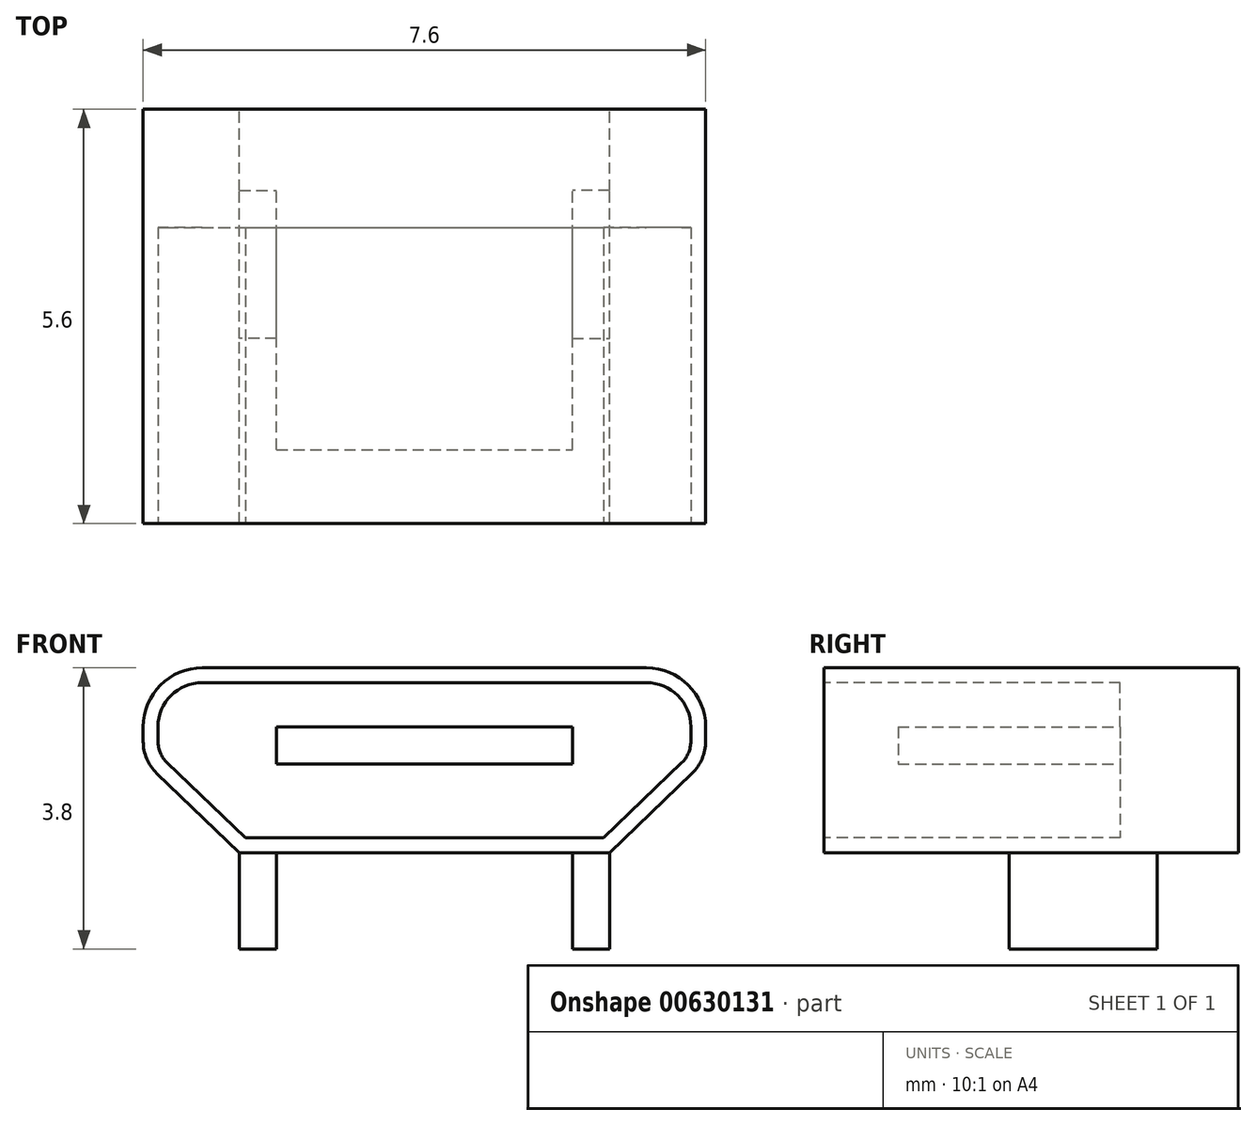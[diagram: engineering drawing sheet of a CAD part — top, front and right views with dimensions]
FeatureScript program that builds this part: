
annotation { "Feature Type Name" : "Feature", "Feature Type Description" : "" }
export const myFeature = defineFeature(function(context is Context, id is Id, definition is map)
    precondition{}
    {
        {
            var Q0;
            Q0=qCreatedBy(makeId("Front.planeOp"),FACE);
            var sketch = newSketch(context, id + "F0", { "sketchPlane" : qUnion([Q0])});
            skLineSegment(sketch, "E0.bottom", {"start": v(0, 0) * mm, "end": v(7.6, 0) * mm, "construction": true});
            skLineSegment(sketch, "E0.top", {"start": v(0, 2.5) * mm, "end": v(7.6, 2.5) * mm, "construction": true});
            skLineSegment(sketch, "E0.left", {"start": v(0, 0) * mm, "end": v(0, 2.5) * mm, "construction": true});
            skLineSegment(sketch, "E0.right", {"start": v(7.6, 0) * mm, "end": v(7.6, 2.5) * mm, "construction": true});
            skLineSegment(sketch, "E1", {"start": v(0, 1.25) * mm, "end": v(1.3, 0) * mm});
            skLineSegment(sketch, "E2", {"start": v(7.6, 1.25) * mm, "end": v(6.3, 0) * mm});
            skLineSegment(sketch, "E3", {"start": v(0, 1.25) * mm, "end": v(0, 2.5) * mm});
            skLineSegment(sketch, "E4", {"start": v(0, 2.5) * mm, "end": v(7.6, 2.5) * mm});
            skLineSegment(sketch, "E5", {"start": v(7.6, 2.5) * mm, "end": v(7.6, 1.25) * mm});
            skLineSegment(sketch, "E6", {"start": v(1.3, 0) * mm, "end": v(6.3, 0) * mm});
            skSolve(sketch);
        }
        {
            var Q0;
            Q0=qSketchRegion(id+"F0",true);
            extrude(context, id + "F1", {"entities" : qUnion([Q0]), "depth" : 5.6 * mm});
        }
        {
            var Q0;
            Q0=makeQuery(id+"F1.opExtrude","SWEPT_EDGE",EDGE,{"disambiguationData":[OSD([sQuery(id+"F0.wireOp",EDGE,"E3"),sQuery(id+"F0.wireOp",EDGE,"E4")])]});
            var Q1;
            Q1=makeQuery(id+"F1.opExtrude","SWEPT_EDGE",EDGE,{"disambiguationData":[OSD([sQuery(id+"F0.wireOp",EDGE,"E4"),sQuery(id+"F0.wireOp",EDGE,"E5")])]});
            fillet(context, id + "F2", {"entities" : qUnion([Q0, Q1]), "radius" : 0.8 * mm, "tangentPropagation" : true, "allowEdgeOverflow" : false});
        }
        {
            var Q0;
            Q0=makeQuery(id+"F1.opExtrude","SWEPT_EDGE",EDGE,{"disambiguationData":[OSD([sQuery(id+"F0.wireOp",EDGE,"E1"),sQuery(id+"F0.wireOp",EDGE,"E3")])]});
            var Q1;
            Q1=makeQuery(id+"F1.opExtrude","SWEPT_EDGE",EDGE,{"disambiguationData":[OSD([sQuery(id+"F0.wireOp",EDGE,"E2"),sQuery(id+"F0.wireOp",EDGE,"E5")])]});
            fillet(context, id + "F3", {"entities" : qUnion([Q0, Q1]), "radius" : 0.6 * mm, "tangentPropagation" : true, "allowEdgeOverflow" : false});
        }
        {
            var Q0;
            Q0=makeQuery(id+"F1.opExtrude","SWEPT_FACE",FACE,{"disambiguationData":[OSD([sQuery(id+"F0.wireOp",EDGE,"E6")])]});
            var sketch = newSketch(context, id + "F4", { "sketchPlane" : qUnion([Q0])});
            skLineSegment(sketch, "E7.right", {"start": v(1.8, 3.1) * mm, "end": v(1.8, 1.1) * mm});
            skLineSegment(sketch, "E8.top", {"start": v(6.3, 1.1) * mm, "end": v(5.8, 1.1) * mm});
            skLineSegment(sketch, "E8.right", {"start": v(5.8, 3.1) * mm, "end": v(5.8, 1.1) * mm});
            skLineSegment(sketch, "E9", {"start": v(1.8, 3.1) * mm, "end": v(1.3, 3.1) * mm});
            skLineSegment(sketch, "E10", {"start": v(5.8, 3.1) * mm, "end": v(6.3, 3.1) * mm});
            skLineSegment(sketch, "E11", {"start": v(6.3, 3.1) * mm, "end": v(6.3, 1.1) * mm});
            skLineSegment(sketch, "E12", {"start": v(1.3, 3.1) * mm, "end": v(1.3, 1.1) * mm});
            skLineSegment(sketch, "E13", {"start": v(1.3, 1.1) * mm, "end": v(1.8, 1.1) * mm});
            skSolve(sketch);
        }
        {
            var Q0;
            Q0=qSketchRegion(id+"F4",true);
            extrude(context, id + "F5", {"entities" : qUnion([Q0]), "operationType" : NewBodyOperationType.ADD, "depth" : 1.3 * mm});
        }
        {
            var Q0;
            Q0=makeQuery(id+"F5.boolean.opBoolean","MERGE",FACE,{"derivedFrom":[makeQuery(id+"F1.opExtrude","CAP_FACE",FACE,{"disambiguationData":[OSD([sQuery(id+"F0.wireOp",EDGE,"E1"),sQuery(id+"F0.wireOp",EDGE,"E2"),sQuery(id+"F0.wireOp",EDGE,"E3"),sQuery(id+"F0.wireOp",EDGE,"E4"),sQuery(id+"F0.wireOp",EDGE,"E5"),sQuery(id+"F0.wireOp",EDGE,"E6")])],"isStart":false}),makeQuery(id+"F5.opExtrude","SWEPT_FACE",FACE,{"disambiguationData":[OSD([sQuery(id+"F4.wireOp",EDGE,"E7.bottom")])]}),makeQuery(id+"F5.opExtrude","SWEPT_FACE",FACE,{"disambiguationData":[OSD([sQuery(id+"F4.wireOp",EDGE,"E8.bottom")])]})]});
            var sketch = newSketch(context, id + "F6", { "sketchPlane" : qUnion([Q0])});
            skLineSegment(sketch, "E14", {"start": v(0.8, 2.3) * mm, "end": v(6.8, 2.3) * mm});
            skLineSegment(sketch, "E15", {"start": v(1.38, 0.2) * mm, "end": v(6.22, 0.2) * mm});
            skArc(sketch, "E16", {"start": v(0.8, 2.3) * mm, "mid": v(0.38, 2.12) * mm, "end": v(0.2, 1.7) * mm});
            skArc(sketch, "E17", {"start": v(7.4, 1.7) * mm, "mid": v(7.22, 2.12) * mm, "end": v(6.8, 2.3) * mm});
            skLineSegment(sketch, "E18", {"start": v(0.32, 1.22) * mm, "end": v(1.38, 0.2) * mm});
            skArc(sketch, "E19", {"start": v(0.2, 1.5) * mm, "mid": v(0.23, 1.35) * mm, "end": v(0.32, 1.22) * mm});
            skArc(sketch, "E20", {"start": v(7.28, 1.22) * mm, "mid": v(7.37, 1.35) * mm, "end": v(7.4, 1.5) * mm});
            skLineSegment(sketch, "E21", {"start": v(7.4, 1.7) * mm, "end": v(7.4, 1.5) * mm});
            skLineSegment(sketch, "E22", {"start": v(7.28, 1.22) * mm, "end": v(6.22, 0.2) * mm});
            skLineSegment(sketch, "E23", {"start": v(0.2, 1.7) * mm, "end": v(0.2, 1.5) * mm});
            skSolve(sketch);
        }
        {
            var Q0;
            Q0=qSketchRegion(id+"F6",true);
            extrude(context, id + "F7", {"entities" : qUnion([Q0]), "operationType" : NewBodyOperationType.REMOVE, "oppositeDirection" : true, "depth" : 4 * mm});
        }
        {
            var Q0;
            Q0=makeQuery(id+"F7.boolean.opBoolean","COPY",FACE,{"derivedFrom":makeQuery(id+"F7.opExtrude","CAP_FACE",FACE,{"disambiguationData":[OSD([sQuery(id+"F6.wireOp",EDGE,"E14"),sQuery(id+"F6.wireOp",EDGE,"E15"),sQuery(id+"F6.wireOp",EDGE,"E16"),sQuery(id+"F6.wireOp",EDGE,"E17"),sQuery(id+"F6.wireOp",EDGE,"E18"),sQuery(id+"F6.wireOp",EDGE,"E19"),sQuery(id+"F6.wireOp",EDGE,"E20"),sQuery(id+"F6.wireOp",EDGE,"E21"),sQuery(id+"F6.wireOp",EDGE,"E22"),sQuery(id+"F6.wireOp",EDGE,"E23")])],"isStart":false})});
            var sketch = newSketch(context, id + "F8", { "sketchPlane" : qUnion([Q0])});
            skLineSegment(sketch, "E24.bottom", {"start": v(1.8, 1.7) * mm, "end": v(5.8, 1.7) * mm});
            skLineSegment(sketch, "E24.top", {"start": v(1.8, 1.2) * mm, "end": v(5.8, 1.2) * mm});
            skLineSegment(sketch, "E24.left", {"start": v(1.8, 1.7) * mm, "end": v(1.8, 1.2) * mm});
            skLineSegment(sketch, "E24.right", {"start": v(5.8, 1.7) * mm, "end": v(5.8, 1.2) * mm});
            skLineSegment(sketch, "E25", {"start": v(3.8, 2.3) * mm, "end": v(3.8, 0.2) * mm, "construction": true});
            skSolve(sketch);
        }
        {
            var Q0;
            Q0=qSketchRegion(id+"F8",true);
            extrude(context, id + "F9", {"entities" : qUnion([Q0]), "operationType" : NewBodyOperationType.ADD, "depth" : 3 * mm});
        }
    });
